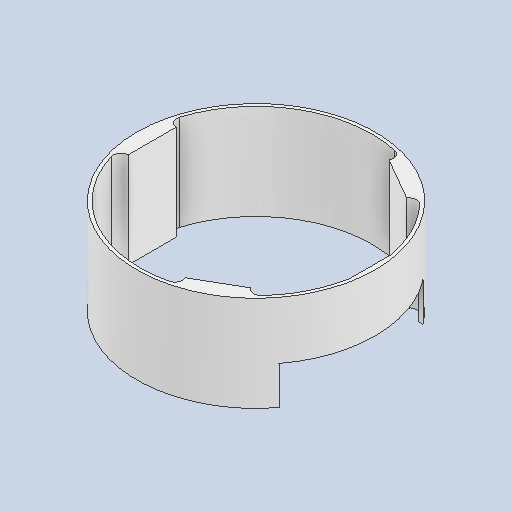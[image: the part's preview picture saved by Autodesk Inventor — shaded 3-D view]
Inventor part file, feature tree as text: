
AUTODESK INVENTOR PART (.ipt)
format: ipt  version: 2023 (Build 270158000, 158)  size: 296,960 bytes
history: native  units: mm
features: extrude x4, sketch x4, other x1, fillet x1
ambient origin geometry x8: Origin, YZ Plane, XZ Plane, XY Plane, X Axis, Y Axis, Z Axis, Center Point
bodies: Body1 (feature_tree)
feature tree (10):
  other  "ソリッド1"
  extrude  "押し出し1"  Depth=250.0mm
  fillet  "フィレット1"  Radius=243.0mm
  extrude  "押し出し4"  Depth=118.86mm
  extrude  "押し出し5"  Depth=10.0mm
  extrude  "押し出し6"  Depth=30.0mm TaperAngle=360.0deg
  sketch  "スケッチ1"
  sketch  "スケッチ4"
  sketch  "スケッチ5"
  sketch  "スケッチ6"
